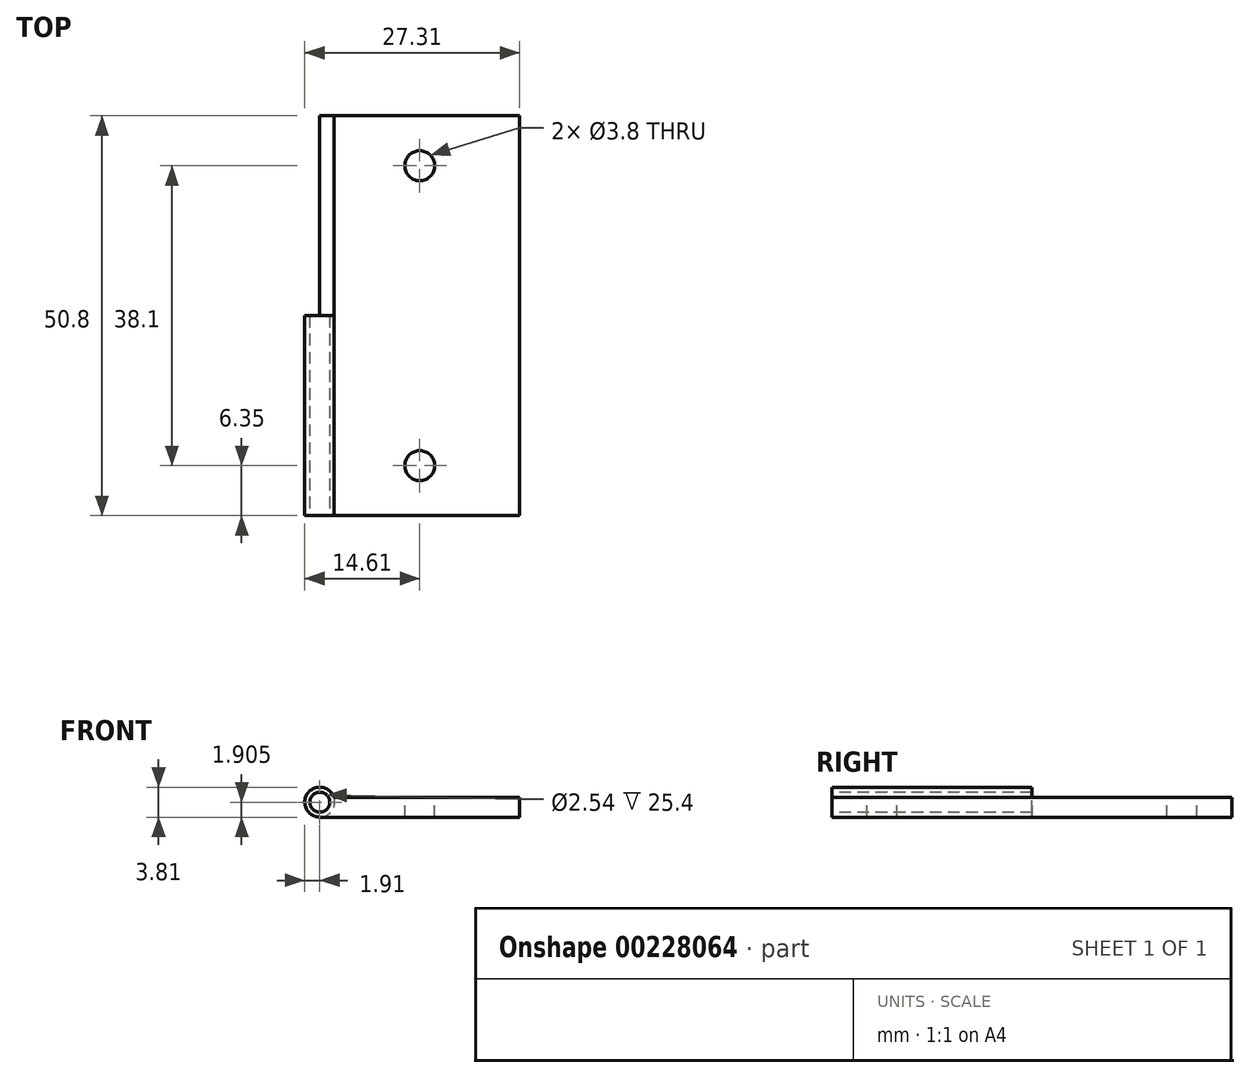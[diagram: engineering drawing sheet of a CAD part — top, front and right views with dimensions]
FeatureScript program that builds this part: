
annotation { "Feature Type Name" : "Feature", "Feature Type Description" : "" }
export const myFeature = defineFeature(function(context is Context, id is Id, definition is map)
    precondition{}
    {
        {
            var Q0;
            Q0=qCreatedBy(makeId("Top.planeOp"),FACE);
            var sketch = newSketch(context, id + "F0", { "sketchPlane" : qUnion([Q0])});
            skLineSegment(sketch, "E0.bottom", {"start": v(0, 0) * mm, "end": v(25.4, 0) * mm});
            skLineSegment(sketch, "E0.top", {"start": v(0, 50.8) * mm, "end": v(25.4, 50.8) * mm});
            skLineSegment(sketch, "E0.left", {"start": v(0, 0) * mm, "end": v(0, 50.8) * mm});
            skLineSegment(sketch, "E0.right", {"start": v(25.4, 0) * mm, "end": v(25.4, 50.8) * mm});
            skSolve(sketch);
        }
        {
            var Q0;
            Q0 = qSketchRegion(id + "F0", true);
            extrude(context, id + "F1", {"entities" : qUnion([Q0]), "depth" : 2.54 * mm});
        }
        {
            var Q0;
            Q0=makeQuery(id+"F1.opExtrude","CAP_FACE",FACE,{"disambiguationData":[OSD([sQuery(id+"F0.wireOp",EDGE,"E0.bottom"),sQuery(id+"F0.wireOp",EDGE,"E0.top"),sQuery(id+"F0.wireOp",EDGE,"E0.left"),sQuery(id+"F0.wireOp",EDGE,"E0.right")])],"isStart":false});
            var sketch = newSketch(context, id + "F2", { "sketchPlane" : qUnion([Q0])});
            skPoint(sketch, "E1", {"position": v(12.7, 44.45) * mm});
            skPoint(sketch, "E2", {"position": v(12.7, 6.35) * mm});
            skLineSegment(sketch, "E3", {"start": v(12.7, 44.45) * mm, "end": v(12.7, 50.8) * mm, "construction": true});
            skLineSegment(sketch, "E4", {"start": v(12.7, 6.35) * mm, "end": v(12.7, 0) * mm, "construction": true});
            skSolve(sketch);
        }
        {
            var Q0;
            Q0=sQuery(id+"F2.wireOp",VERTEX,"E1");
            var Q1;
            Q1=sQuery(id+"F2.wireOp",VERTEX,"E2");
            var Q2;
            Q2=makeQuery(id+"F1.opExtrude","SWEPT_BODY",BODY,{"disambiguationData":[OSD([sQuery(id+"F0.wireOp",EDGE,"E0.bottom"),sQuery(id+"F0.wireOp",EDGE,"E0.top"),sQuery(id+"F0.wireOp",EDGE,"E0.left"),sQuery(id+"F0.wireOp",EDGE,"E0.right")])]});
            hole(context, id + "F3", {"style" : HoleStyle.SIMPLE, "endStyle" : HoleEndStyle.THROUGH, "standardTappedOrClearance" : lookupTablePath({ "standard" : "ANSI", "fit" : "Normal (ASME)", "size" : "#6", "type" : "Clearance" }), "standardBlindInLast" : lookupTablePath({ "fit" : "Free", "standard" : "ANSI", "size" : "#6", "type" : "Clearance" }), "holeDiameter" : 3.8 * mm, "locations" : qUnion([Q0, Q1]), "scope" : qUnion([Q2]), "isTappedThrough" : true});
        }
        {
            var Q0;
            Q0=makeQuery(id+"F1.opExtrude","SWEPT_FACE",FACE,{"disambiguationData":[OSD([sQuery(id+"F0.wireOp",EDGE,"E0.bottom")])]});
            var sketch = newSketch(context, id + "F4", { "sketchPlane" : qUnion([Q0])});
            skCircle(sketch, "E5", {"center": v(0, 1.9) * mm, "radius": 1.9 * mm});
            skSolve(sketch);
        }
        {
            var Q0;
            Q0 = qSketchRegion(id + "F4", true);
            var Q1;
            Q1=makeQuery(id+"F1.opExtrude","SWEPT_FACE",FACE,{"disambiguationData":[OSD([sQuery(id+"F0.wireOp",EDGE,"E0.top")])]});
            extrude(context, id + "F5", {"entities" : qUnion([Q0]), "operationType" : NewBodyOperationType.ADD, "oppositeDirection" : true, "endBoundEntityFace" : qUnion([Q1]), "depth" : 25.4 * mm});
        }
        {
            var Q0;
            Q0=makeQuery(id+"F5.boolean.opBoolean","MERGE",FACE,{"derivedFrom":[makeQuery(id+"F1.opExtrude","SWEPT_FACE",FACE,{"disambiguationData":[OSD([sQuery(id+"F0.wireOp",EDGE,"E0.bottom")])]}),makeQuery(id+"F5.opExtrude","CAP_FACE",FACE,{"disambiguationData":[OSD([sQuery(id+"F4.wireOp",EDGE,"E5")])],"isStart":true})]});
            var sketch = newSketch(context, id + "F6", { "sketchPlane" : qUnion([Q0])});
            skCircle(sketch, "E6", {"center": v(0, 1.9) * mm, "radius": 1.27 * mm});
            skSolve(sketch);
        }
        {
            var Q0;
            Q0 = qSketchRegion(id + "F6", true);
            var Q1;
            Q1=makeQuery(id+"F5.opExtrude","CAP_FACE",FACE,{"disambiguationData":[OSD([sQuery(id+"F4.wireOp",EDGE,"E5")])],"isStart":false});
            extrude(context, id + "F7", {"entities" : qUnion([Q0]), "operationType" : NewBodyOperationType.REMOVE, "endBound" : BoundingType.UP_TO_SURFACE, "oppositeDirection" : true, "endBoundEntityFace" : qUnion([Q1]), "depth" : 25.4 * mm});
        }
        {
            var Q0;
            Q0 = qSketchRegion(id + "F4", true);
            extrude(context, id + "F8", {"entities" : qUnion([Q0]), "operationType" : NewBodyOperationType.REMOVE, "oppositeDirection" : true, "depth" : 50.8 * mm, "hasSecondDirection" : true, "secondDirectionOppositeDirection" : true, "secondDirectionDepth" : 25.4 * mm});
        }
    });
